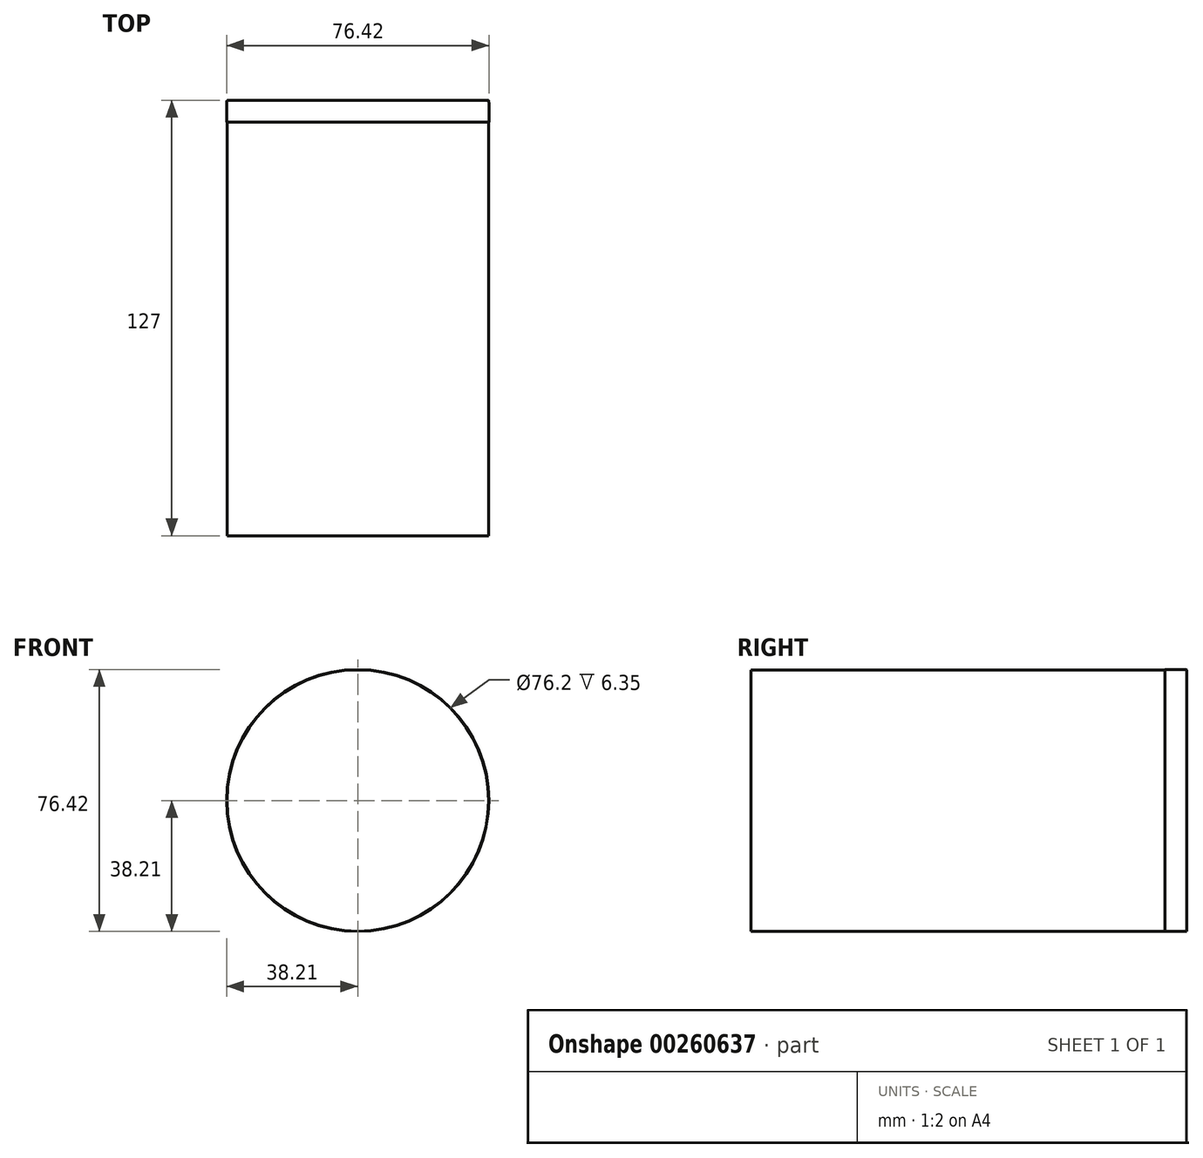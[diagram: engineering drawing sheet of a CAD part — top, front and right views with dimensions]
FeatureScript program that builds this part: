
annotation { "Feature Type Name" : "Feature", "Feature Type Description" : "" }
export const myFeature = defineFeature(function(context is Context, id is Id, definition is map)
    precondition{}
    {
        {
            var Q0;
            Q0=qCreatedBy(makeId("Front.planeOp"),FACE);
            var sketch = newSketch(context, id + "F0", { "sketchPlane" : qUnion([Q0])});
            skCircle(sketch, "E0", {"center": v(0, 0) * mm, "radius": 38.1 * mm});
            skCircle(sketch, "E1", {"center": v(0, 0) * mm, "radius": 41.28 * mm});
            skCircle(sketch, "E2", {"center": v(0, 0) * mm, "radius": 38.21 * mm});
            skSolve(sketch);
        }
        {
            var Q0;
            Q0=makeQuery(id+"F0.imprint","IMPRINT",FACE,{"disambiguationData":[TD([[makeQuery(id+"F0.imprint","IMPRINT",EDGE,{"derivedFrom":sQuery(id+"F0.wireOp",EDGE,"E0")}),-1.0]])]});
            extrude(context, id + "F1", {"entities" : qUnion([Q0]), "depth" : 6.35 * mm});
        }
        {
            var Q0;
            Q0=makeQuery(id+"F0.imprint","IMPRINT",FACE,{"disambiguationData":[TD([[makeQuery(id+"F0.imprint","IMPRINT",EDGE,{"derivedFrom":sQuery(id+"F0.wireOp",EDGE,"E0")}),1.0]])]});
            extrude(context, id + "F2", {"entities" : qUnion([Q0]), "depth" : 127 * mm});
        }
        {
            var Q0;
            Q0=sQuery(id+"F0.wireOp",EDGE,"E2");
            var Q1;
            Q1=sQuery(id+"F0.wireOp",EDGE,"E1");
            extrude(context, id + "F3", {"bodyType" : ToolBodyType.SURFACE, "surfaceEntities" : qUnion([Q0, Q1]), "depth" : 25.4 * mm});
        }
        {
            var Q0;
            Q0=makeQuery(id+"F1.opExtrude","CAP_EDGE",EDGE,{"disambiguationData":[OSD([sQuery(id+"F0.wireOp",EDGE,"E2")])],"isStart":true});
            fillet(context, id + "F4", {"entities" : qUnion([Q0]), "radius" : 5.08 * mm, "tangentPropagation" : true, "allowEdgeOverflow" : false});
        }
    });
